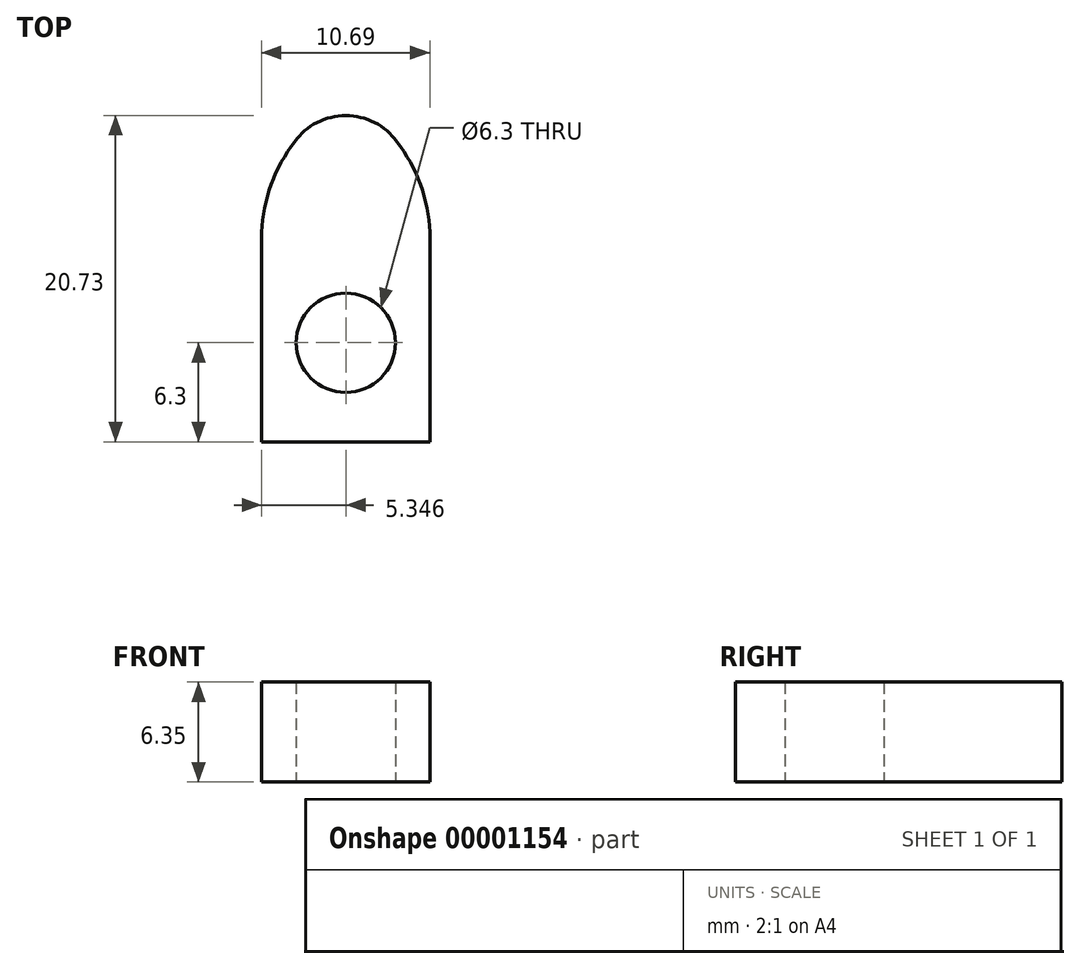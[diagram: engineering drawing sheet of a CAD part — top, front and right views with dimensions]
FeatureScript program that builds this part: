
annotation { "Feature Type Name" : "Feature", "Feature Type Description" : "" }
export const myFeature = defineFeature(function(context is Context, id is Id, definition is map)
    precondition{}
    {
        {
            var Q0;
            Q0=qCreatedBy(makeId("Top.planeOp"),FACE);
            var sketch = newSketch(context, id + "F0", { "sketchPlane" : qUnion([Q0])});
            skLineSegment(sketch, "E0", {"start": v(0, 0) * mm, "end": v(10.7, 0) * mm});
            skLineSegment(sketch, "E1", {"start": v(10.7, 0) * mm, "end": v(10.7, 16.14) * mm});
            skLineSegment(sketch, "E2", {"start": v(10.7, 16.14) * mm, "end": v(5.35, 23.6) * mm});
            skLineSegment(sketch, "E3", {"start": v(5.35, 23.6) * mm, "end": v(0, 16.14) * mm});
            skLineSegment(sketch, "E4", {"start": v(0, 16.14) * mm, "end": v(0, 0) * mm});
            skLineSegment(sketch, "E5", {"start": v(5.35, 0) * mm, "end": v(5.35, 6.3) * mm});
            skCircle(sketch, "E6", {"center": v(5.35, 6.3) * mm, "radius": 3.15 * mm});
            skSolve(sketch);
        }
        {
            var Q0;
            Q0=makeQuery(id+"F0.imprint","IMPRINT",FACE,{"disambiguationData":[TD([[makeQuery(id+"F0.imprint","IMPRINT",EDGE,{"derivedFrom":sQuery(id+"F0.wireOp",EDGE,"E0")}),1.0]])]});
            extrude(context, id + "F1", {"entities" : qUnion([Q0]), "depth" : 6.35 * mm});
        }
        {
            var Q0;
            Q0=makeQuery(id+"F1.opExtrude","SWEPT_EDGE",EDGE,{"disambiguationData":[OSD([sQuery(id+"F0.wireOp",EDGE,"E2"),sQuery(id+"F0.wireOp",EDGE,"E3")])]});
            fillet(context, id + "F2", {"entities" : qUnion([Q0]), "radius" : 4 * mm, "tangentPropagation" : true, "allowEdgeOverflow" : false});
        }
        {
            var Q0;
            Q0=makeQuery(id+"F1.opExtrude","SWEPT_EDGE",EDGE,{"disambiguationData":[OSD([sQuery(id+"F0.wireOp",EDGE,"E3"),sQuery(id+"F0.wireOp",EDGE,"E4")])]});
            var Q1;
            Q1=makeQuery(id+"F1.opExtrude","SWEPT_EDGE",EDGE,{"disambiguationData":[OSD([sQuery(id+"F0.wireOp",EDGE,"E1"),sQuery(id+"F0.wireOp",EDGE,"E2")])]});
            fillet(context, id + "F3", {"entities" : qUnion([Q0, Q1]), "radius" : 10 * mm, "tangentPropagation" : true, "allowEdgeOverflow" : false});
        }
        {
            var Q0;
            Q0=sQuery(id+"F0.wireOp",EDGE,"E6");
            extrude(context, id + "F4", {"bodyType" : ToolBodyType.SURFACE, "surfaceEntities" : qUnion([Q0]), "depth" : 10 * mm});
        }
        {
            var Q0;
            Q0=makeQuery(id+"F4.opExtrude","SWEPT_BODY",BODY,{"disambiguationData":[OSD([sQuery(id+"F0.wireOp",EDGE,"E6")])]});
            var Q1;
            Q1=qCreatedBy(makeId("Top.planeOp"),FACE);
            transform(context, id + "F5", {"entities" : qUnion([Q0]), "transformType" : TransformType.TRANSLATION_DISTANCE, "transformDirection" : qUnion([Q1]), "distance" : 2 * mm, "oppositeDirection" : true, "oppositeX" : false, "oppositeY" : false, "oppositeZ" : false, "makeCopy" : false});
        }
    });
